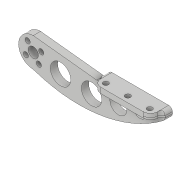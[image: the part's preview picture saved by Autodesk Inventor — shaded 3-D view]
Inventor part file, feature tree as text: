
AUTODESK INVENTOR PART (.ipt)
format: ipt  version: 2018 (Build 220112000, 112)  size: 219,648 bytes
history: native  units: in
note: dims shown in document units (in); Inventor stores cm internally (conversion verified against a paired STEP export)
features: sketch x6, fillet x4, extrude x3, hole x2
ambient origin geometry x8: Origin, YZ Plane, XZ Plane, XY Plane, X Axis, Y Axis, Z Axis, Center Point
bodies: Solid1 (feature_tree)
feature tree (15):
  sketch  "Sketch1"  dims[d0=1.0in d1=0.35in d2=0.0in]
  extrude  "Extrusion1"  Depth=0.35in
  fillet  "Fillet1"  [1 undecoded]
  hole  "Hole1"  [1 undecoded]
  fillet  "Fillet2"  Radius=0.25in
  extrude  "Extrusion2"  Depth=0.25in
  extrude  "Extrusion3"  Depth=0.25in TaperAngle=0.0deg
  fillet  "Fillet3"  Radius=0.1875in
  fillet  "Fillet4"  Radius=0.375in
  hole  "Hole2"  [1 undecoded]
  sketch  "Sketch2"  dims[d3=0.25in d4=0.0in d5=0.25in d6=0.0in]
  sketch  "Sketch3"  dims[d7=0.125in]
  sketch  "Sketch4"  dims[d8=0.177in d9=0.5in d10=0.332in d11=0.25in d12=0.5635in d13=0.75in d14=0.8108in d15=0.7in]
  sketch  "Sketch5"  dims[d16=0.7in d17=0.25in d18=0.0in d19=0.1875in d20=0.375in d21=0.0in]
  sketch  "Sketch6"  dims[d22=0.15in d23=0.25in d24=0.75in d25=0.75in d26=0.2in d27=0.2in d28=0.2in d29=0.7218in d30=0.7218in d31=0.177in d32=0.5in d33=0.332in d34=0.25in d35=0.5635in d36=0.75in d37=0.8108in]
note: 3 required parameter values undecoded (feature->parameter linkage not recoverable at this tier; creation-order binding heuristic only, values carry confidence <= 0.55)
